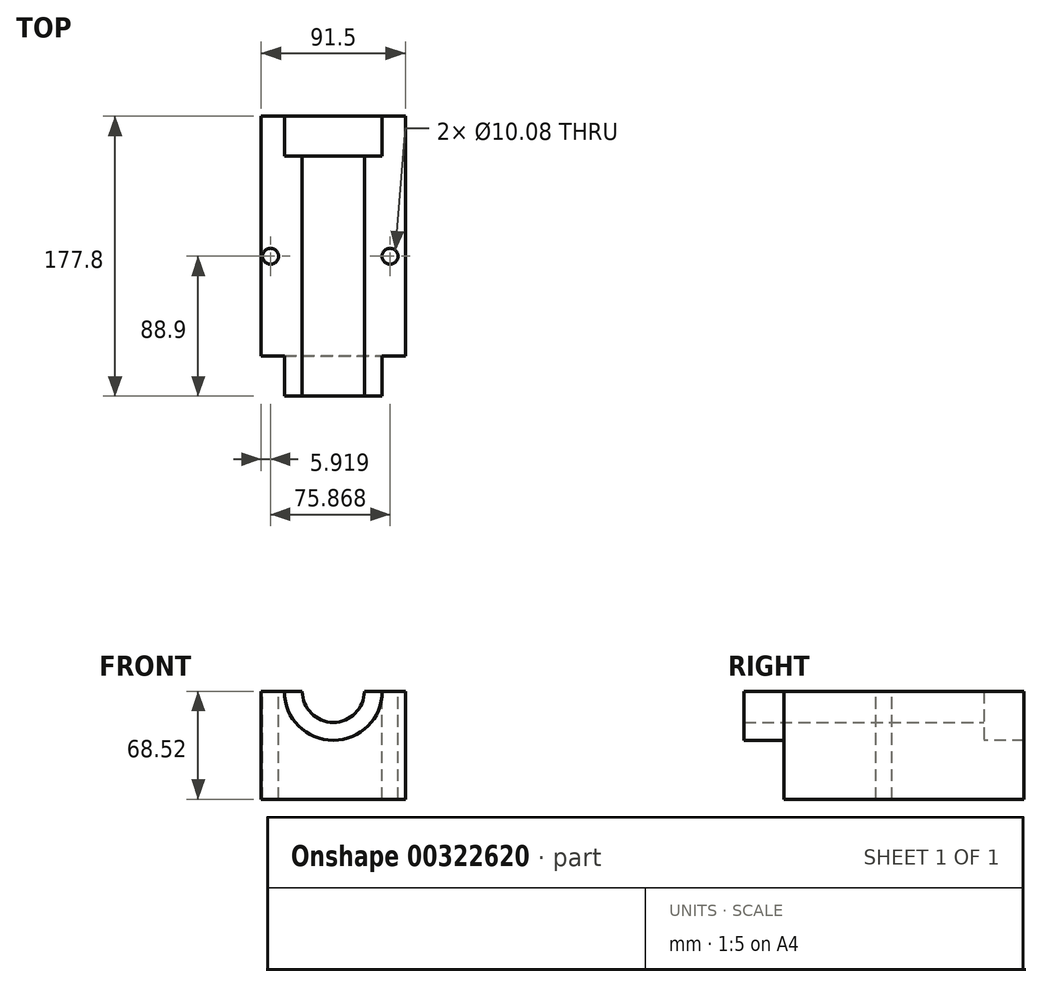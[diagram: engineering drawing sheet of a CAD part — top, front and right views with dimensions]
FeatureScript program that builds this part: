
annotation { "Feature Type Name" : "Feature", "Feature Type Description" : "" }
export const myFeature = defineFeature(function(context is Context, id is Id, definition is map)
    precondition{}
    {
        {
            var Q0;
            Q0=qCreatedBy(makeId("Front.planeOp"),FACE);
            var sketch = newSketch(context, id + "F0", { "sketchPlane" : qUnion([Q0])});
            skLineSegment(sketch, "E0.bottom", {"start": v(45.75, 34.26) * mm, "end": v(-45.75, 34.26) * mm});
            skLineSegment(sketch, "E0.top", {"start": v(45.75, -34.26) * mm, "end": v(-45.75, -34.26) * mm});
            skLineSegment(sketch, "E0.left", {"start": v(45.75, 34.26) * mm, "end": v(45.75, -34.26) * mm});
            skLineSegment(sketch, "E0.right", {"start": v(-45.75, 34.26) * mm, "end": v(-45.75, -34.26) * mm});
            skPoint(sketch, "E0.middle", {"position": v(0, 0) * mm});
            skSolve(sketch);
        }
        {
            var Q0;
            Q0=makeQuery(id+"F0.imprint","IMPRINT",FACE,{"disambiguationData":[TD([[makeQuery(id+"F0.imprint","IMPRINT",EDGE,{"derivedFrom":sQuery(id+"F0.wireOp",EDGE,"E0.bottom")}),1.0]])]});
            extrude(context, id + "F1", {"entities" : qUnion([Q0]), "endBound" : BoundingType.SYMMETRIC, "depth" : 127 * mm});
        }
        {
            var Q0;
            Q0=makeQuery(id+"F1.opExtrude","CAP_FACE",FACE,{"disambiguationData":[OSD([sQuery(id+"F0.wireOp",EDGE,"E0.bottom"),sQuery(id+"F0.wireOp",EDGE,"E0.top"),sQuery(id+"F0.wireOp",EDGE,"E0.left"),sQuery(id+"F0.wireOp",EDGE,"E0.right")])],"isStart":false});
            var sketch = newSketch(context, id + "F2", { "sketchPlane" : qUnion([Q0])});
            skArc(sketch, "E1", {"start": v(-31.1, 34.26) * mm, "mid": v(0, 3.17) * mm, "end": v(31.1, 34.26) * mm});
            skArc(sketch, "E2", {"start": v(-19.7, 34.26) * mm, "mid": v(0, 14.55) * mm, "end": v(19.7, 34.26) * mm});
            skLineSegment(sketch, "E3.0", {"start": v(45.75, 34.26) * mm, "end": v(-45.75, 34.26) * mm});
            skSolve(sketch);
        }
        {
            var Q0;
            {var subQ0=sQuery(id+"F2.wireOp",EDGE,"E1");Q0=makeQuery(id+"F2.imprint","IMPRINT",FACE,{"disambiguationData":[TD([[makeQuery(id+"F2.imprint","IMPRINT",EDGE,{"derivedFrom":subQ0}),1.0]])]});}
            extrude(context, id + "F3", {"entities" : qUnion([Q0]), "operationType" : NewBodyOperationType.ADD, "depth" : 25.4 * mm});
        }
        {
            var Q0;
            Q0=makeQuery(id+"F3.opExtrude","CAP_FACE",FACE,{"disambiguationData":[OSD([sQuery(id+"F2.wireOp",EDGE,"E1"),sQuery(id+"F2.wireOp",EDGE,"E2"),sQuery(id+"F2.wireOp",EDGE,"E3.0")])],"isStart":false});
            var sketch = newSketch(context, id + "F4", { "sketchPlane" : qUnion([Q0])});
            skArc(sketch, "E4.0", {"start": v(-19.7, 34.26) * mm, "mid": v(0, 14.55) * mm, "end": v(19.7, 34.26) * mm});
            skLineSegment(sketch, "E5.0", {"start": v(19.7, 34.26) * mm, "end": v(-19.7, 34.26) * mm});
            skSolve(sketch);
        }
        {
            var Q0;
            Q0 = qSketchRegion(id + "F4", true);
            extrude(context, id + "F5", {"entities" : qUnion([Q0]), "operationType" : NewBodyOperationType.REMOVE, "endBound" : BoundingType.THROUGH_ALL, "oppositeDirection" : true, "depth" : 25.4 * mm});
        }
        {
            var Q0;
            Q0=makeQuery(id+"F1.opExtrude","CAP_FACE",FACE,{"disambiguationData":[OSD([sQuery(id+"F0.wireOp",EDGE,"E0.bottom"),sQuery(id+"F0.wireOp",EDGE,"E0.top"),sQuery(id+"F0.wireOp",EDGE,"E0.left"),sQuery(id+"F0.wireOp",EDGE,"E0.right")])],"isStart":true});
            var sketch = newSketch(context, id + "F6", { "sketchPlane" : qUnion([Q0])});
            skArc(sketch, "E6.0", {"start": v(31.1, 34.26) * mm, "mid": v(0, 3.17) * mm, "end": v(-31.1, 34.26) * mm});
            skLineSegment(sketch, "E7.0", {"start": v(19.7, 34.26) * mm, "end": v(45.75, 34.26) * mm});
            skLineSegment(sketch, "E8.0", {"start": v(-45.75, 34.26) * mm, "end": v(-19.7, 34.26) * mm});
            skSolve(sketch);
        }
        {
            var Q0;
            Q0 = qSketchRegion(id + "F6", true);
            var Q1;
            {var subQ0=sQuery(id+"F6.wireOp",EDGE,"E6.0");Q1=makeQuery(id+"F6.imprint","IMPRINT",FACE,{"disambiguationData":[TD([[makeQuery(id+"F6.imprint","IMPRINT",EDGE,{"derivedFrom":subQ0}),-1.0]])]});}
            extrude(context, id + "F7", {"entities" : qUnion([Q0, Q1]), "operationType" : NewBodyOperationType.ADD, "depth" : 25.4 * mm});
        }
        {
            var Q0;
            {var subQ0=sQuery(id+"F2.wireOp",EDGE,"E1");var subQ1=sQuery(id+"F0.wireOp",EDGE,"E0.right");var subQ4=sQuery(id+"F0.wireOp",EDGE,"E0.bottom");var subQ5=sQuery(id+"F2.wireOp",EDGE,"E3.0");Q0=makeQuery(id+"F7.boolean.opBoolean","MERGE",FACE,{"derivedFrom":[makeQuery(id+"F5.boolean.opBoolean","SPLIT",FACE,{"disambiguationData":[TD([makeQuery(id+"F1.opExtrude","SWEPT_FACE",FACE,{"disambiguationData":[OSD([subQ1])]})])],"derivedFrom":makeQuery(id+"F3.boolean.opBoolean","MERGE",FACE,{"derivedFrom":[makeQuery(id+"F1.opExtrude","SWEPT_FACE",FACE,{"disambiguationData":[OSD([subQ4])]}),makeQuery(id+"F3.opExtrude","SWEPT_FACE",FACE,{"disambiguationData":[OSD([subQ5]),TDD([makeQuery(id+"F2.imprint","IMPRINT",EDGE,{"disambiguationData":[TD([[makeQuery(id+"F2.imprint","INTERSECT",VERTEX,{"disambiguationData":[OD(1.0)],"derivedFrom":[subQ0,subQ5]}),-1.0]])],"derivedFrom":subQ5})])]}),makeQuery(id+"F3.opExtrude","SWEPT_FACE",FACE,{"disambiguationData":[OSD([subQ5]),TDD([makeQuery(id+"F2.imprint","IMPRINT",EDGE,{"disambiguationData":[TD([[makeQuery(id+"F2.imprint","INTERSECT",VERTEX,{"disambiguationData":[OD(0.0)],"derivedFrom":[subQ0,subQ5]}),1.0]])],"derivedFrom":subQ5})])]})]})}),makeQuery(id+"F7.opExtrude","SWEPT_FACE",FACE,{"disambiguationData":[OSD([sQuery(id+"F6.wireOp",EDGE,"E7.0")])]})]});}
            var sketch = newSketch(context, id + "F8", { "sketchPlane" : qUnion([Q0])});
            skCircle(sketch, "E9", {"center": v(-39.83, 0) * mm, "radius": 5.04 * mm});
            skCircle(sketch, "E10", {"center": v(36.04, 0) * mm, "radius": 5.04 * mm});
            skSolve(sketch);
        }
        {
            var Q0;
            Q0=makeQuery(id+"F8.imprint","IMPRINT",FACE,{"disambiguationData":[TD([[makeQuery(id+"F8.imprint","IMPRINT",EDGE,{"derivedFrom":sQuery(id+"F8.wireOp",EDGE,"E10")}),1.0]])]});
            var Q1;
            Q1=makeQuery(id+"F8.imprint","IMPRINT",FACE,{"disambiguationData":[TD([[makeQuery(id+"F8.imprint","IMPRINT",EDGE,{"derivedFrom":sQuery(id+"F8.wireOp",EDGE,"E9")}),1.0]])]});
            extrude(context, id + "F9", {"entities" : qUnion([Q0, Q1]), "operationType" : NewBodyOperationType.REMOVE, "endBound" : BoundingType.THROUGH_ALL, "oppositeDirection" : true, "depth" : 25.4 * mm});
        }
    });
